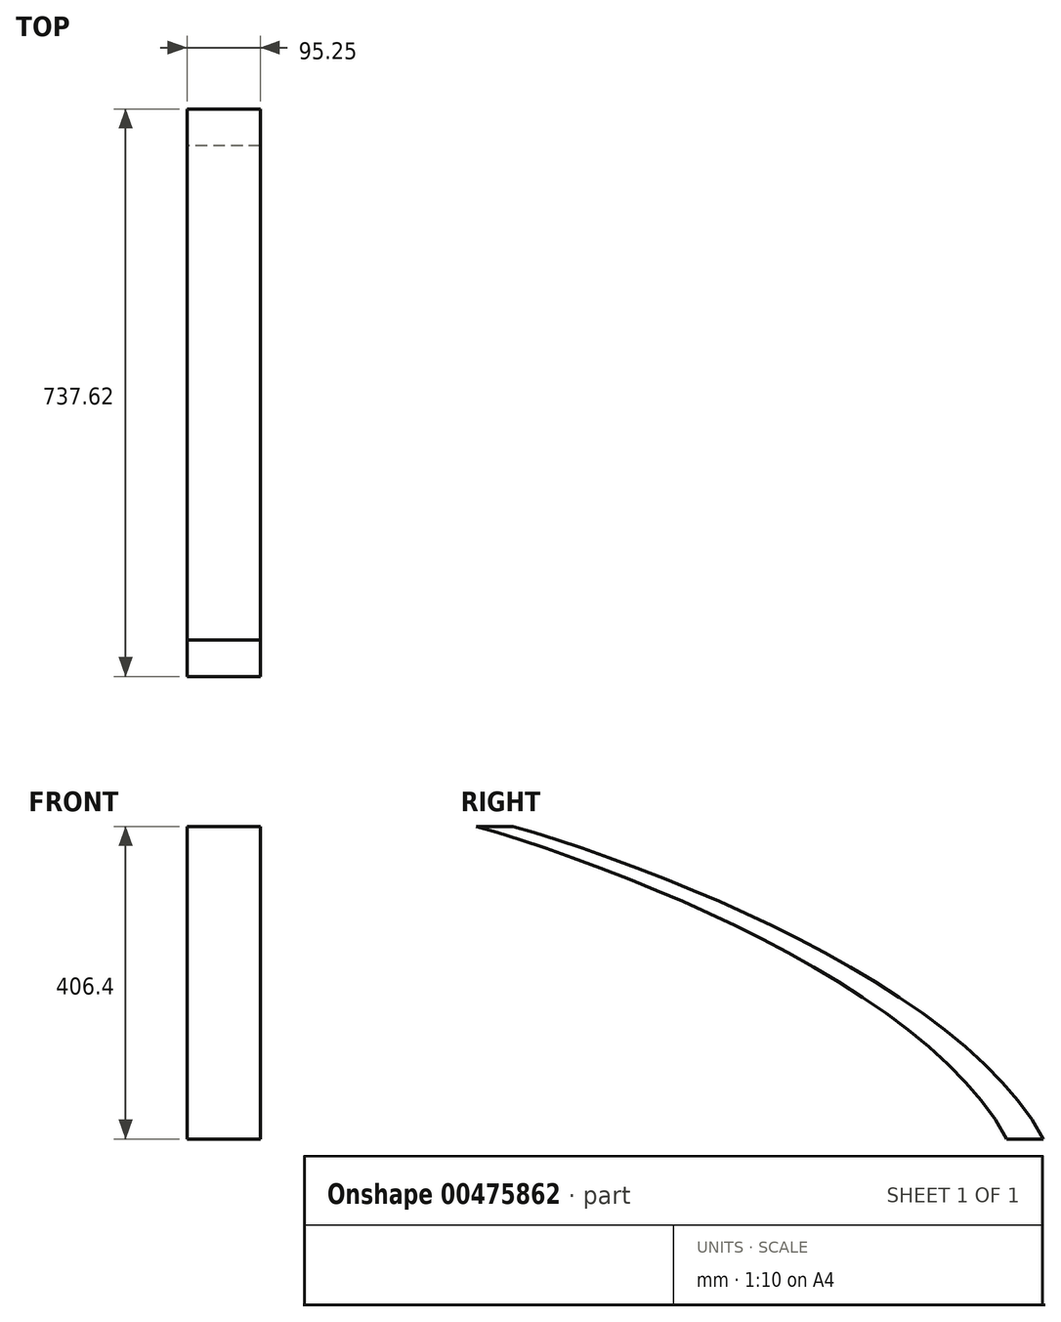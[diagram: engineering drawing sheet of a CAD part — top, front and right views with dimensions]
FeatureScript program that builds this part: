
annotation { "Feature Type Name" : "Feature", "Feature Type Description" : "" }
export const myFeature = defineFeature(function(context is Context, id is Id, definition is map)
    precondition{}
    {
        {
            var Q0;
            Q0=qCreatedBy(makeId("Front.planeOp"),FACE);
            var sketch = newSketch(context, id + "F0", { "sketchPlane" : qUnion([Q0])});
            skLineSegment(sketch, "E0", {"start": v(209.38, -129.63) * mm, "end": v(266.53, -129.63) * mm});
            skFitSpline(sketch, "E1", {"points": [v(-423.46, 276.77) * mm, v(266.53, -129.63) * mm], "startDerivative": vector(266.7, -304.8) * mm, "endDerivative": vector(325.52, -609.6) * mm});
            skPoint(sketch, "E2.endSnap0", {"position": v(-51.73, -54.47) * mm});
            skLineSegment(sketch, "E3", {"start": v(158.03, 73.57) * mm, "end": v(153.17, -158.97) * mm});
            skFitSpline(sketch, "E4", {"points": [v(-423.46, 276.77) * mm, v(266.53, -129.63) * mm], "startDerivative": vector(533.4, -152.4) * mm, "endDerivative": vector(325.52, -609.6) * mm});
            skLineSegment(sketch, "E5", {"start": v(266.53, -129.63) * mm, "end": v(266.53, 22.77) * mm});
            skLineSegment(sketch, "E6", {"start": v(266.53, 22.77) * mm, "end": v(158.03, 25.04) * mm});
            skLineSegment(sketch, "E7", {"start": v(266.53, -129.63) * mm, "end": v(266.53, 73.57) * mm});
            skLineSegment(sketch, "E8", {"start": v(266.53, 73.57) * mm, "end": v(158.03, 73.57) * mm});
            skSolve(sketch);
        }
        {
            var Q0;
            Q0=qCreatedBy(makeId("Top.planeOp"),FACE);
            var sketch = newSketch(context, id + "F1", { "sketchPlane" : qUnion([Q0])});
            skLineSegment(sketch, "E9.bottom", {"start": v(28.58, -38.1) * mm, "end": v(-19.05, -38.1) * mm});
            skLineSegment(sketch, "E9.top", {"start": v(28.57, 57.15) * mm, "end": v(-19.05, 57.15) * mm});
            skLineSegment(sketch, "E9.left", {"start": v(28.58, -38.1) * mm, "end": v(28.58, 57.15) * mm});
            skLineSegment(sketch, "E9.right", {"start": v(-19.05, -38.1) * mm, "end": v(-19.05, 57.15) * mm});
            skPoint(sketch, "E9.middle", {"position": v(4.76, 9.53) * mm});
            skSolve(sketch);
        }
        {
            var Q0;
            Q0=makeQuery(id+"F1.imprint","IMPRINT",FACE,{"disambiguationData":[TD([[makeQuery(id+"F1.imprint","IMPRINT",EDGE,{"derivedFrom":sQuery(id+"F1.wireOp",EDGE,"E9.bottom")}),-1.0]])]});
            extrude(context, id + "F2", {"entities" : qUnion([Q0]), "depth" : 203.2 * mm});
        }
        {
            var Q0;
            Q0=makeQuery(id+"F2.opExtrude","CAP_FACE",FACE,{"disambiguationData":[OSD([sQuery(id+"F1.wireOp",EDGE,"E9.bottom"),sQuery(id+"F1.wireOp",EDGE,"E9.top"),sQuery(id+"F1.wireOp",EDGE,"E9.left"),sQuery(id+"F1.wireOp",EDGE,"E9.right")])],"isStart":false});
            var Q1;
            Q1=sQuery(id+"F0.wireOp",EDGE,"E4");
            sweep(context, id + "F3", {"profiles" : qUnion([Q0]), "path" : qUnion([Q1]), "keepProfileOrientation" : true});
        }
        {
            var Q0;
            Q0=makeQuery(id+"F2.opExtrude","SWEPT_BODY",BODY,{"disambiguationData":[OSD([sQuery(id+"F1.wireOp",EDGE,"E9.bottom"),sQuery(id+"F1.wireOp",EDGE,"E9.top"),sQuery(id+"F1.wireOp",EDGE,"E9.left"),sQuery(id+"F1.wireOp",EDGE,"E9.right")])]});
            deleteBodies(context, id + "F4", {"entities" : qUnion([Q0])});
        }
        {
            var Q0;
            Q0=qCreatedBy(makeId("Front.planeOp"),FACE);
            var sketch = newSketch(context, id + "F5", { "sketchPlane" : qUnion([Q0])});
            skLineSegment(sketch, "E10", {"start": v(0, 0) * mm, "end": v(0, 73) * mm});
            skSolve(sketch);
        }
        {
            var Q0;
            Q0=makeQuery(id+"F3.opSweep","SWEPT_BODY",BODY,{"disambiguationData":[OSD([sQuery(id+"F0.wireOp",EDGE,"E4"),sQuery(id+"F1.wireOp",EDGE,"E9.bottom"),sQuery(id+"F1.wireOp",EDGE,"E9.top"),sQuery(id+"F1.wireOp",EDGE,"E9.left"),sQuery(id+"F1.wireOp",EDGE,"E9.right")])]});
            var Q1;
            Q1=sQuery(id+"F5.wireOp",EDGE,"E10");
            transform(context, id + "F6", {"entities" : qUnion([Q0]), "transformType" : TransformType.ROTATION, "transformAxis" : qUnion([Q1]), "angle" : 90 * degree, "makeCopy" : false});
        }
    });
